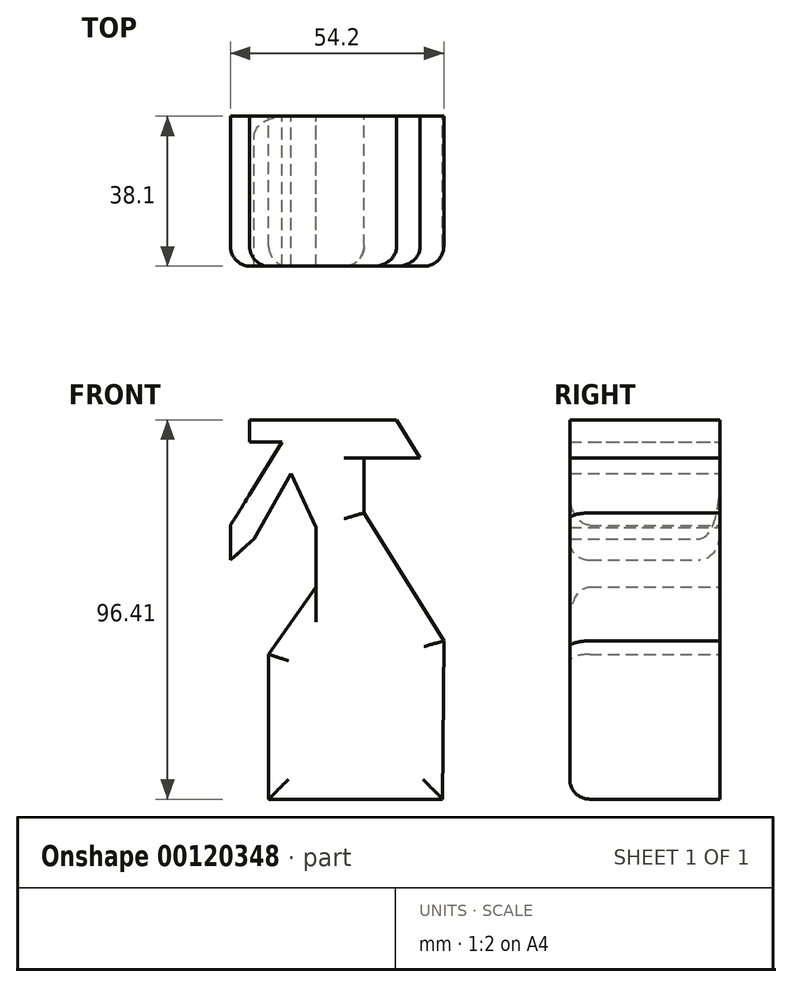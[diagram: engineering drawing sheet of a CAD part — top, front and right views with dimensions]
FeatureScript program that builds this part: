
annotation { "Feature Type Name" : "Feature", "Feature Type Description" : "" }
export const myFeature = defineFeature(function(context is Context, id is Id, definition is map)
    precondition{}
    {
        {
            var Q0;
            Q0=qCreatedBy(makeId("Front.planeOp"),FACE);
            var sketch = newSketch(context, id + "F0", { "sketchPlane" : qUnion([Q0])});
            skLineSegment(sketch, "E0", {"start": v(-29.38, -44.07) * mm, "end": v(14.83, -44.07) * mm});
            skLineSegment(sketch, "E1", {"start": v(-29.38, -44.07) * mm, "end": v(-29.38, -7.27) * mm});
            skLineSegment(sketch, "E2", {"start": v(-29.38, -7.27) * mm, "end": v(-17.4, 9.84) * mm});
            skLineSegment(sketch, "E3", {"start": v(-17.4, 9.84) * mm, "end": v(-17.4, 24.96) * mm});
            skLineSegment(sketch, "E4", {"start": v(-17.4, 24.96) * mm, "end": v(-23.67, 38.65) * mm});
            skLineSegment(sketch, "E5", {"start": v(-23.67, 38.65) * mm, "end": v(-33.09, 22.1) * mm});
            skLineSegment(sketch, "E6", {"start": v(-33.09, 22.1) * mm, "end": v(-39.08, 16.69) * mm});
            skLineSegment(sketch, "E7", {"start": v(-39.08, 16.69) * mm, "end": v(-39.08, 25.53) * mm});
            skLineSegment(sketch, "E8", {"start": v(-39.08, 25.53) * mm, "end": v(-25.96, 46.64) * mm});
            skLineSegment(sketch, "E9", {"start": v(-25.96, 46.64) * mm, "end": v(-34.23, 46.64) * mm});
            skLineSegment(sketch, "E10", {"start": v(-34.23, 46.64) * mm, "end": v(-34.23, 52.34) * mm});
            skLineSegment(sketch, "E11", {"start": v(-34.23, 52.34) * mm, "end": v(3.14, 52.34) * mm});
            skLineSegment(sketch, "E12", {"start": v(3.14, 52.34) * mm, "end": v(9.13, 42.64) * mm});
            skLineSegment(sketch, "E13", {"start": v(9.13, 42.64) * mm, "end": v(-5.13, 42.64) * mm});
            skLineSegment(sketch, "E14", {"start": v(-5.13, 42.64) * mm, "end": v(-5.13, 28.67) * mm});
            skLineSegment(sketch, "E15", {"start": v(-5.13, 28.67) * mm, "end": v(15.12, -3.85) * mm});
            skLineSegment(sketch, "E16", {"start": v(15.12, -3.85) * mm, "end": v(14.83, -44.07) * mm});
            skSolve(sketch);
        }
        {
            var Q0;
            Q0 = qSketchRegion(id + "F0", true);
            extrude(context, id + "F1", {"entities" : qUnion([Q0]), "depth" : 12.7 * mm});
        }
        {
            var Q0;
            Q0=makeQuery(id+"F0.imprint","IMPRINT",FACE,{"disambiguationData":[TD([[makeQuery(id+"F0.imprint","IMPRINT",EDGE,{"derivedFrom":sQuery(id+"F0.wireOp",EDGE,"E0")}),1.0]])]});
            var Q1;
            Q1=makeQuery(id+"F1.opExtrude","CAP_FACE",FACE,{"disambiguationData":[OSD([sQuery(id+"F0.wireOp",EDGE,"E0"),sQuery(id+"F0.wireOp",EDGE,"E1"),sQuery(id+"F0.wireOp",EDGE,"E2"),sQuery(id+"F0.wireOp",EDGE,"E3"),sQuery(id+"F0.wireOp",EDGE,"E4"),sQuery(id+"F0.wireOp",EDGE,"E5"),sQuery(id+"F0.wireOp",EDGE,"E6"),sQuery(id+"F0.wireOp",EDGE,"E7"),sQuery(id+"F0.wireOp",EDGE,"E8"),sQuery(id+"F0.wireOp",EDGE,"E9"),sQuery(id+"F0.wireOp",EDGE,"E10"),sQuery(id+"F0.wireOp",EDGE,"E11"),sQuery(id+"F0.wireOp",EDGE,"E12"),sQuery(id+"F0.wireOp",EDGE,"E13"),sQuery(id+"F0.wireOp",EDGE,"E14"),sQuery(id+"F0.wireOp",EDGE,"E15"),sQuery(id+"F0.wireOp",EDGE,"E16")])],"isStart":false});
            var Q2;
            Q2=makeQuery(id+"F1.opExtrude","CAP_FACE",FACE,{"disambiguationData":[OSD([sQuery(id+"F0.wireOp",EDGE,"E0"),sQuery(id+"F0.wireOp",EDGE,"E1"),sQuery(id+"F0.wireOp",EDGE,"E2"),sQuery(id+"F0.wireOp",EDGE,"E3"),sQuery(id+"F0.wireOp",EDGE,"E4"),sQuery(id+"F0.wireOp",EDGE,"E5"),sQuery(id+"F0.wireOp",EDGE,"E6"),sQuery(id+"F0.wireOp",EDGE,"E7"),sQuery(id+"F0.wireOp",EDGE,"E8"),sQuery(id+"F0.wireOp",EDGE,"E9"),sQuery(id+"F0.wireOp",EDGE,"E10"),sQuery(id+"F0.wireOp",EDGE,"E11"),sQuery(id+"F0.wireOp",EDGE,"E12"),sQuery(id+"F0.wireOp",EDGE,"E13"),sQuery(id+"F0.wireOp",EDGE,"E14"),sQuery(id+"F0.wireOp",EDGE,"E15"),sQuery(id+"F0.wireOp",EDGE,"E16")])],"isStart":true});
            extrude(context, id + "F2", {"entities" : qUnion([Q0, Q1, Q2]), "operationType" : NewBodyOperationType.ADD, "depth" : 25.4 * mm});
        }
        {
            var Q0;
            {var subQ0=sQuery(id+"F0.wireOp",EDGE,"E7");Q0=makeQuery(id+"F2.opExtrude","CAP_EDGE",EDGE,{"disambiguationData":[OSD([subQ0]),TDD([makeQuery(id+"F1.opExtrude","CAP_EDGE",EDGE,{"disambiguationData":[OSD([subQ0])],"isStart":false})])],"isStart":false});}
            var Q1;
            Q1=makeQuery(id+"F1.opExtrude","CAP_EDGE",EDGE,{"disambiguationData":[OSD([sQuery(id+"F0.wireOp",EDGE,"E6")])],"isStart":true});
            var Q2;
            {var subQ0=sQuery(id+"F0.wireOp",EDGE,"E12");Q2=makeQuery(id+"F2.opExtrude","CAP_EDGE",EDGE,{"disambiguationData":[OSD([subQ0]),TDD([makeQuery(id+"F1.opExtrude","CAP_EDGE",EDGE,{"disambiguationData":[OSD([subQ0])],"isStart":false})])],"isStart":false});}
            var Q3;
            {var subQ0=sQuery(id+"F0.wireOp",EDGE,"E15");Q3=makeQuery(id+"F2.opExtrude","CAP_EDGE",EDGE,{"disambiguationData":[OSD([subQ0]),TDD([makeQuery(id+"F1.opExtrude","CAP_EDGE",EDGE,{"disambiguationData":[OSD([subQ0])],"isStart":false})])],"isStart":false});}
            var Q4;
            {var subQ0=sQuery(id+"F0.wireOp",EDGE,"E14");Q4=makeQuery(id+"F2.opExtrude","CAP_EDGE",EDGE,{"disambiguationData":[OSD([subQ0]),TDD([makeQuery(id+"F1.opExtrude","CAP_EDGE",EDGE,{"disambiguationData":[OSD([subQ0])],"isStart":false})])],"isStart":false});}
            var Q5;
            {var subQ0=sQuery(id+"F0.wireOp",EDGE,"E16");Q5=makeQuery(id+"F2.opExtrude","CAP_EDGE",EDGE,{"disambiguationData":[OSD([subQ0]),TDD([makeQuery(id+"F1.opExtrude","CAP_EDGE",EDGE,{"disambiguationData":[OSD([subQ0])],"isStart":false})])],"isStart":false});}
            var Q6;
            {var subQ0=sQuery(id+"F0.wireOp",EDGE,"E10");Q6=makeQuery(id+"F2.opExtrude","CAP_EDGE",EDGE,{"disambiguationData":[OSD([subQ0]),TDD([makeQuery(id+"F1.opExtrude","CAP_EDGE",EDGE,{"disambiguationData":[OSD([subQ0])],"isStart":false})])],"isStart":false});}
            var Q7;
            {var subQ0=sQuery(id+"F0.wireOp",EDGE,"E2");Q7=makeQuery(id+"F2.opExtrude","CAP_EDGE",EDGE,{"disambiguationData":[OSD([subQ0]),TDD([makeQuery(id+"F1.opExtrude","CAP_EDGE",EDGE,{"disambiguationData":[OSD([subQ0])],"isStart":false})])],"isStart":false});}
            var Q8;
            {var subQ0=sQuery(id+"F0.wireOp",EDGE,"E1");Q8=makeQuery(id+"F2.opExtrude","CAP_EDGE",EDGE,{"disambiguationData":[OSD([subQ0]),TDD([makeQuery(id+"F1.opExtrude","CAP_EDGE",EDGE,{"disambiguationData":[OSD([subQ0])],"isStart":false})])],"isStart":false});}
            var Q9;
            {var subQ0=sQuery(id+"F0.wireOp",EDGE,"E0");Q9=makeQuery(id+"F2.opExtrude","CAP_EDGE",EDGE,{"disambiguationData":[OSD([subQ0]),TDD([makeQuery(id+"F1.opExtrude","CAP_EDGE",EDGE,{"disambiguationData":[OSD([subQ0])],"isStart":false})])],"isStart":false});}
            fillet(context, id + "F3", {"entities" : qUnion([Q0, Q1, Q2, Q3, Q4, Q5, Q6, Q7, Q8, Q9]), "radius" : 5.08 * mm, "tangentPropagation" : true, "allowEdgeOverflow" : false});
        }
    });
